# Revit family: RUSHWORK_400-П_DN50-300
name_source: partatom
category: Арматура трубопроводов
units: mm (PartAtom-declared; Revit-internal decimal feet)

## family parameters
Всегда вертикально = Нет
На основе рабочей плоскости = Нет
Общий = Нет
При загрузке вырезать с полостями = Нет
Размер круглого соединителя = Использовать диаметр
Тип детали = Клапан - Вставляется

## types (8) — shared parameters
ADSK_Единица измерения = шт
ADSK_Завод-изготовитель = ООО ТД "РАШВОРК"
URL = https://rwru.ru
Изготовитель = ООО ТД "РАШВОРК"
Материал корпус = чугун GJL-250 (GG25)
Ц = 168 мм
zero-valued in all types: Отметка по умолчанию

## per-type parameters (varying)
| type | ADSK_Код изделия | ADSK_Масса | D_Eвыдавливания | D_Hвыдавливания | D_Конектор | D_клапана | F штока | L_клапана | Высота штока | Н-L_выдавливание | Н_выдавливание | Направление потока |
| Клапан обратный двухстворчатый РАШВОРК 400-050-16-П, DN050, PN16, корпус - GJL-250 (GG25), пластины - CF8M, уплотнение - EPDM, М/Ф | 400-050-16-П | 1.5 | 45 мм | 66 мм | 50 мм | 101 мм | 15 мм | 27 мм | 86 мм | 39 мм | 15 мм | 111 мм |
| Клапан обратный двухстворчатый РАШВОРК 400-065-16-П, DN065, PN16, корпус - GJL-250 (GG25), пластины - CF8M, уплотнение - EPDM, М/Ф | 400-065-16-П | 2 | 59 мм | 80 мм | 65 мм | 119 мм | 17 мм | 27 мм | 104 мм | 37 мм | 17 мм | 129 мм |
| Клапан обратный двухстворчатый РАШВОРК 400-080-16-П, DN080, PN16, корпус - GJL-250 (GG25), пластины - CF8M, уплотнение - EPDM, М/Ф | 400-080-16-П | 2.6 | 72 мм | 95 мм | 80 мм | 133 мм | 19 мм | 29 мм | 118 мм | 38 мм | 19 мм | 143 мм |
| Клапан обратный двухстворчатый РАШВОРК 400-100-16-П, DN100, PN16, корпус - GJL-250 (GG25), пластины - CF8M, уплотнение - EPDM, М/Ф | 400-100-16-П | 4.1 | 90 мм | 117 мм | 100 мм | 164 мм | 23 мм | 32 мм | 149 мм | 41 мм | 23 мм | 174 мм |
| Клапан обратный двухстворчатый РАШВОРК 400-150-16-П, DN150, PN16, корпус - GJL-250 (GG25), пластины - CF8M, уплотнение - EPDM, М/Ф | 400-150-16-П | 7.8 | 135 мм | 170 мм | 150 мм | 220 мм | 28 мм | 38 мм | 205 мм | 48 мм | 28 мм | 230 мм |
| Клапан обратный двухстворчатый РАШВОРК 400-200-16-П, DN200, PN16, корпус - GJL-250 (GG25), пластины - CF8M, уплотнение - EPDM, М/Ф | 400-200-16-П | 16.1 | 175 мм | 224 мм | 200 мм | 275 мм | 38 мм | 48 мм | 260 мм | 57 мм | 38 мм | 285 мм |
| Клапан обратный двухстворчатый РАШВОРК 400-250-16-П, DN250, PN16, корпус - GJL-250 (GG25), пластины - CF8M, уплотнение - EPDM, М/Ф | 400-250-16-П | 25.1 | 215 мм | 255 мм | 250 мм | 328 мм | 43 мм | 53 мм | 313 мм | 62 мм | 43 мм | 338 мм |
| Клапан обратный двухстворчатый РАШВОРК 400-300-16-П, DN300, PN16, корпус - GJL-250 (GG25), пластины - CF8M, уплотнение - EPDM, М/Ф | 400-300-16-П | 33.9 | 224 мм | 302 мм | 300 мм | 378 мм | 50 мм | 72 мм | 363 мм | 93 мм | 50 мм | 388 мм |

note: column(s) folded — value = type name in every type: ADSK_Наименование
